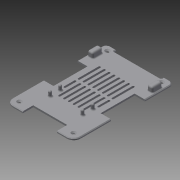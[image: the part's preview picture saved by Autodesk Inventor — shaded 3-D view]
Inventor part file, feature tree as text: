
AUTODESK INVENTOR PART (.ipt)
format: ipt  version: 2015 (Build 190159000, 159)  size: 507,904 bytes
history: native  units: mm
features: fillet x9, extrude x8, sketch x8, hole x4, chamfer x2, pattern_linear x1
ambient origin geometry x8: Origin, YZ Plane, XZ Plane, XY Plane, X Axis, Y Axis, Z Axis, Center Point
bodies: Volumenkörper1 (feature_tree)
feature tree (32):
  extrude  "Extrusion1"  Depth=10.0mm
  fillet  "Rundung2"  Radius=2.5mm
  fillet  "Rundung3"  Radius=10.0mm
  extrude  "Extrusion2"  Depth=3.0mm
  extrude  "Extrusion11"  Depth=3.0mm
  fillet  "Rundung9"  Radius=3.0mm
  extrude  "Extrusion13"  Depth=140.0mm
  pattern_linear  "Rechteckige Anordnung1"  Count1=9  [1 undecoded]
  chamfer  "Fase1"  Distance=10.0mm
  extrude  "Extrusion14"  Depth=1.5mm TaperAngle=0.0deg
  fillet  "Rundung10"  Radius=4.0mm
  extrude  "Extrusion15"  Depth=4.0mm
  fillet  "Rundung11"  Radius=15.1mm
  fillet  "Rundung12"  Radius=50.1mm
  extrude  "Extrusion16"  Depth=1.5mm
  chamfer  "Fase2"  Distance=50.1mm
  hole  "Bohrung6"  [1 undecoded]
  hole  "Bohrung7"  [1 undecoded]
  hole  "Bohrung8"  [1 undecoded]
  hole  "Bohrung9"  [1 undecoded]
  extrude  "Extrusion18"  Depth=1.5mm
  fillet  "Rundung16"  Radius=10.0mm
  fillet  "Rundung17"  Radius=10.0mm
  fillet  "Rundung18"  Radius=30.0mm
  sketch  "Skizze1"  dims[d0=145.0mm d1=100.0mm d2=2.5mm d3=0.0mm d10=10.0mm]
  sketch  "Skizze3"  dims[d11=5.0mm d12=3.0mm]
  sketch  "Skizze10"  dims[d14=3.0mm d19=3.0mm d22=3.0mm]
  sketch  "Skizze12"  dims[d23=140.0mm d25=140.0mm]
  sketch  "Skizze13"  dims[d30=10.0mm]
  sketch  "Skizze14"  dims[d33=10.0mm d34=90.0mm]
  sketch  "Skizze15"  dims[d37=10.0mm]
  sketch  "Skizze17"  dims[d42=90.0mm d44=10.0mm d45=6.0mm d46=0.0mm d154=4.0mm d155=4.0mm d162=15.1mm d163=50.1mm d164=15.1mm d165=50.1mm d167=4.95mm d168=15.1mm d171=50.1mm d187=10.0mm d188=0.0mm d190=1.0mm d191=10.0mm d192=10.0mm d239=30.0mm d240=30.0mm d241=6.0mm d242=3.0mm d243=3.0mm d244=47.0mm d245=25.0mm d246=25.0mm d247=10.0mm d248=0.0mm d249=80.0mm d251=7.15mm d252=0.5mm d253=2.0mm d254=45.0deg d291=4.0mm d292=4.0mm d293=4.0mm d294=4.0mm d297=4.0mm d298=4.0mm d299=41.0mm d300=41.0mm d301=24.0mm d302=24.0mm d303=4.0mm d304=4.0mm d305=24.0mm d306=24.0mm d307=11.0mm d308=11.0mm d309=8.0mm d310=0.0mm d311=2.0mm d312=15.0mm d313=15.0mm d314=2.5mm d315=0.0mm d316=2.0mm d317=2.0mm d318=0.05mm d319=0.05mm d320=0.1mm d321=0.05mm d322=0.05mm d323=0.1mm d324=0.05mm d325=0.05mm d326=0.1mm d327=10.0mm d328=0.0mm d329=1.0mm d330=2.0mm d331=45.0deg d332=10.0mm d333=10.0mm d334=3.4mm d335=6.0mm d336=7.0mm d337=2.0mm d338=90.0deg d339=8.0mm d340=20.594885mm d341=10.0mm d342=10.0mm d343=3.4mm d344=6.0mm d345=7.0mm d346=2.0mm d347=90.0deg d348=8.0mm d349=20.594885mm d350=8.0mm d351=10.0mm d352=3.4mm d353=6.0mm d354=7.0mm d355=2.0mm d356=90.0deg d357=8.0mm d358=20.594885mm d359=8.0mm d360=10.0mm d361=3.4mm d362=6.0mm d363=7.0mm d364=2.0mm d365=90.0deg d366=8.0mm d367=20.594885mm d378=8.0mm d379=8.0mm d380=15.0mm d381=15.0mm d382=15.0mm d383=15.0mm d384=2.0mm d385=2.0mm d386=8.0mm d387=0.0mm d388=2.5mm d389=2.5mm d390=1.5mm]
note: 5 required parameter values undecoded (feature->parameter linkage not recoverable at this tier; creation-order binding heuristic only, values carry confidence <= 0.55)
